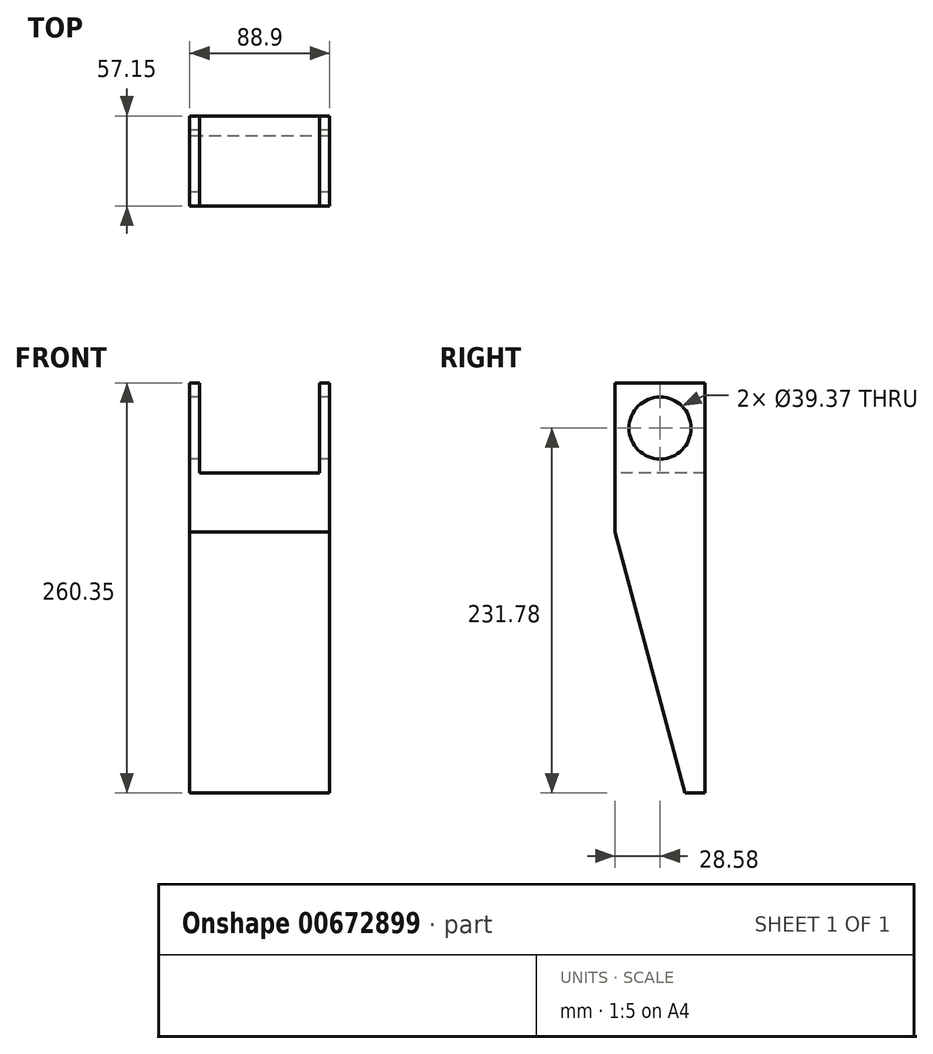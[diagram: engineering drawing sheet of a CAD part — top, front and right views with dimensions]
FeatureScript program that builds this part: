
annotation { "Feature Type Name" : "Feature", "Feature Type Description" : "" }
export const myFeature = defineFeature(function(context is Context, id is Id, definition is map)
    precondition{}
    {
        {
            var Q0;
            Q0=qCreatedBy(makeId("Right.planeOp"),FACE);
            var sketch = newSketch(context, id + "F0", { "sketchPlane" : qUnion([Q0])});
            skCircle(sketch, "E0", {"center": v(0, 0) * mm, "radius": 19.69 * mm});
            skLineSegment(sketch, "E1.bottom", {"start": v(-28.57, 28.57) * mm, "end": v(28.58, 28.57) * mm});
            skLineSegment(sketch, "E1.top", {"start": v(-28.58, -28.57) * mm, "end": v(28.57, -28.57) * mm});
            skLineSegment(sketch, "E1.left", {"start": v(-28.57, 28.57) * mm, "end": v(-28.58, -28.57) * mm});
            skLineSegment(sketch, "E1.right", {"start": v(28.58, 28.57) * mm, "end": v(28.57, -28.57) * mm});
            skLineSegment(sketch, "E2.top", {"start": v(-28.58, -231.78) * mm, "end": v(28.58, -231.78) * mm});
            skLineSegment(sketch, "E2.left", {"start": v(-28.58, -28.57) * mm, "end": v(-28.58, -231.78) * mm});
            skLineSegment(sketch, "E2.right", {"start": v(28.57, -28.57) * mm, "end": v(28.57, -231.78) * mm});
            skSolve(sketch);
        }
        {
            var Q0;
            Q0=makeQuery(id+"F0.imprint","IMPRINT",FACE,{"disambiguationData":[TD([[makeQuery(id+"F0.imprint","IMPRINT",EDGE,{"derivedFrom":sQuery(id+"F0.wireOp",EDGE,"E1.top")}),-1.0]])]});
            extrude(context, id + "F1", {"entities" : qUnion([Q0]), "depth" : 88.9 * mm, "offsetDistance" : 25.4 * mm});
        }
        {
            var Q0;
            Q0=makeQuery(id+"F0.imprint","IMPRINT",FACE,{"disambiguationData":[TD([[makeQuery(id+"F0.imprint","IMPRINT",EDGE,{"derivedFrom":sQuery(id+"F0.wireOp",EDGE,"E0")}),-1.0]])]});
            extrude(context, id + "F2", {"entities" : qUnion([Q0]), "operationType" : NewBodyOperationType.ADD, "depth" : 6.35 * mm, "offsetDistance" : 25.4 * mm});
        }
        {
            var Q0;
            Q0=makeQuery(id+"F1.opExtrude","SWEPT_FACE",FACE,{"disambiguationData":[OSD([sQuery(id+"F0.wireOp",EDGE,"E1.top")])]});
            var sketch = newSketch(context, id + "F3", { "sketchPlane" : qUnion([Q0])});
            skLineSegment(sketch, "E3.bottom", {"start": v(88.9, 28.57) * mm, "end": v(82.55, 28.57) * mm});
            skLineSegment(sketch, "E3.top", {"start": v(88.9, -28.58) * mm, "end": v(82.55, -28.58) * mm});
            skLineSegment(sketch, "E3.left", {"start": v(88.9, 28.57) * mm, "end": v(88.9, -28.58) * mm});
            skLineSegment(sketch, "E3.right", {"start": v(82.55, 28.57) * mm, "end": v(82.55, -28.58) * mm});
            skSolve(sketch);
        }
        {
            var Q0;
            Q0=makeQuery(id+"F3.imprint","IMPRINT",FACE,{"disambiguationData":[TD([[makeQuery(id+"F3.imprint","IMPRINT",EDGE,{"derivedFrom":sQuery(id+"F3.wireOp",EDGE,"E3.bottom")}),1.0]])]});
            extrude(context, id + "F4", {"entities" : qUnion([Q0]), "operationType" : NewBodyOperationType.ADD, "depth" : 57.15 * mm, "offsetDistance" : 25.4 * mm});
        }
        {
            var Q0;
            Q0=makeQuery(id+"F4.opExtrude","SWEPT_FACE",FACE,{"disambiguationData":[OSD([sQuery(id+"F3.wireOp",EDGE,"E3.right")])]});
            var sketch = newSketch(context, id + "F5", { "sketchPlane" : qUnion([Q0])});
            skCircle(sketch, "E4", {"center": v(0, 0) * mm, "radius": 19.69 * mm});
            skSolve(sketch);
        }
        {
            var Q0;
            Q0=makeQuery(id+"F5.imprint","IMPRINT",FACE,{"disambiguationData":[TD([[makeQuery(id+"F5.imprint","IMPRINT",EDGE,{"derivedFrom":sQuery(id+"F5.wireOp",EDGE,"E4")}),1.0]])]});
            extrude(context, id + "F6", {"entities" : qUnion([Q0]), "operationType" : NewBodyOperationType.REMOVE, "oppositeDirection" : true, "depth" : 6.35 * mm, "offsetDistance" : 25.4 * mm});
        }
        {
            var Q0;
            Q0=makeQuery(id+"F1.opExtrude","SWEPT_EDGE",EDGE,{"disambiguationData":[OSD([sQuery(id+"F0.wireOp",EDGE,"E2.top"),sQuery(id+"F0.wireOp",EDGE,"E2.left")])]});
            chamfer(context, id + "F7", {"entities" : qUnion([Q0]), "chamferType" : ChamferType.OFFSET_ANGLE, "width" : 44.45 * mm, "oppositeDirection" : false, "angle" : 75 * degree, "tangentPropagation" : true});
        }
    });
